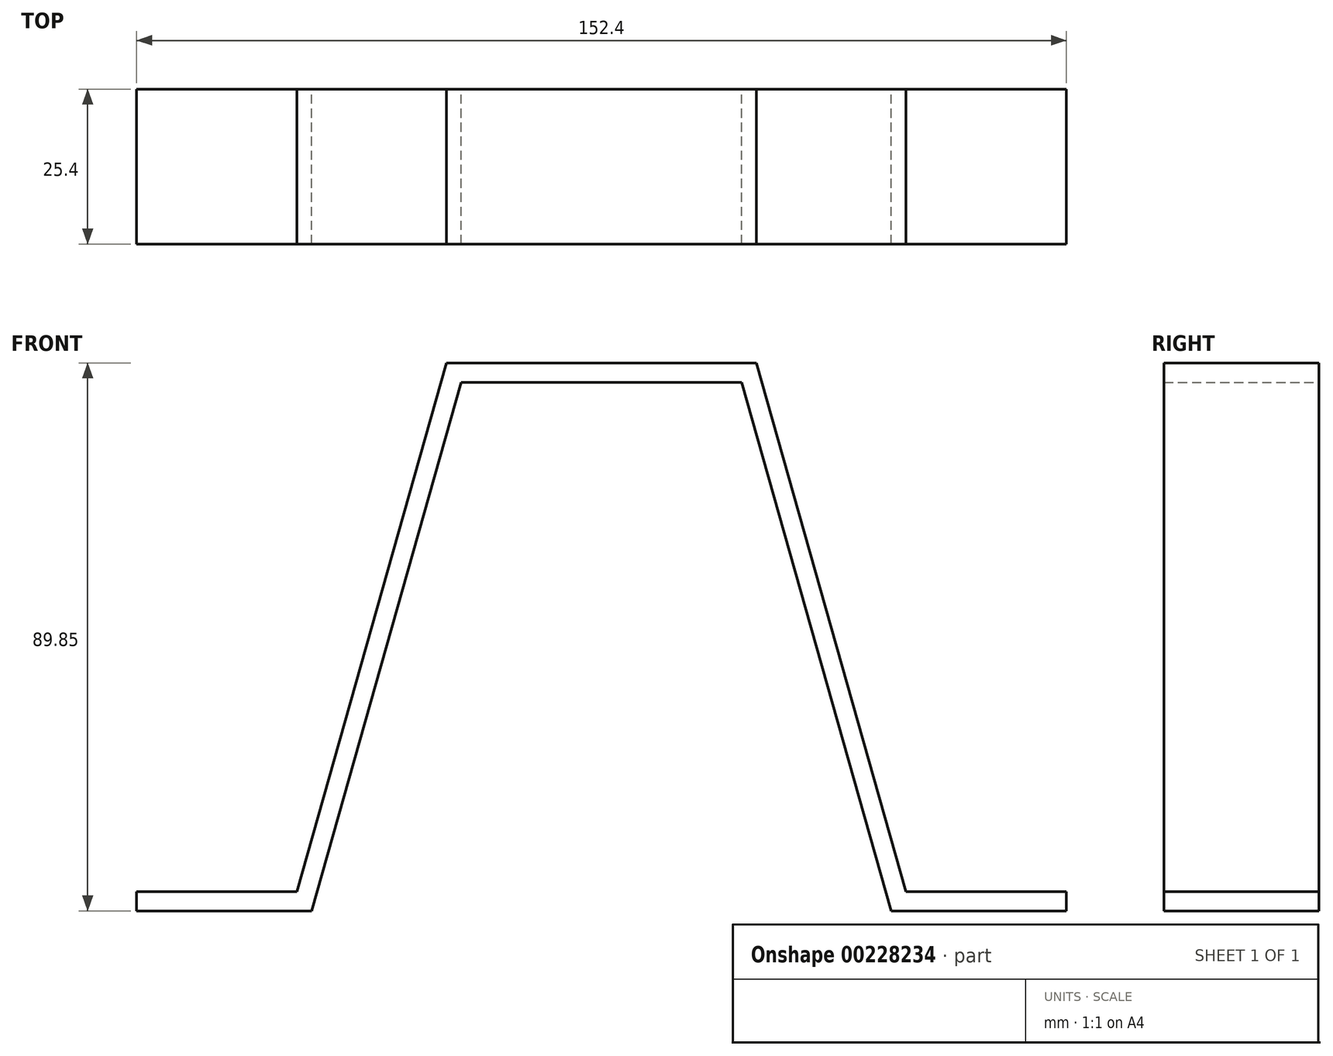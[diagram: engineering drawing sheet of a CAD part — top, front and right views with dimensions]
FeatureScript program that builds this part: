
annotation { "Feature Type Name" : "Feature", "Feature Type Description" : "" }
export const myFeature = defineFeature(function(context is Context, id is Id, definition is map)
    precondition{}
    {
        {
            var Q0;
            Q0=qCreatedBy(makeId("Front.planeOp"),FACE);
            var sketch = newSketch(context, id + "F0", { "sketchPlane" : qUnion([Q0])});
            skLineSegment(sketch, "E0", {"start": v(0, 0) * mm, "end": v(50.8, 0) * mm});
            skLineSegment(sketch, "E1", {"start": v(0, 0) * mm, "end": v(0, 89.85) * mm});
            skLineSegment(sketch, "E2", {"start": v(0, 89.85) * mm, "end": v(25.4, 89.85) * mm});
            skLineSegment(sketch, "E3", {"start": v(25.4, 89.85) * mm, "end": v(50.8, 0) * mm});
            skLineSegment(sketch, "E4.MirrorCS", {"start": v(0, 0) * mm, "end": v(-50.8, 0) * mm});
            skLineSegment(sketch, "E5.MirrorCS", {"start": v(-25.4, 89.85) * mm, "end": v(-50.8, 0) * mm});
            skLineSegment(sketch, "E6.MirrorCS", {"start": v(0, 89.85) * mm, "end": v(-25.4, 89.85) * mm});
            skLineSegment(sketch, "E7.0", {"start": v(-23, 86.68) * mm, "end": v(-47.75, -0.87) * mm});
            skLineSegment(sketch, "E7.1", {"start": v(0, 86.68) * mm, "end": v(-23, 86.68) * mm});
            skLineSegment(sketch, "E7.2", {"start": v(0, 86.68) * mm, "end": v(23, 86.68) * mm});
            skLineSegment(sketch, "E7.3", {"start": v(23, 86.68) * mm, "end": v(60.38, -45.54) * mm});
            skSolve(sketch);
        }
        {
            var Q0;
            {var subQ1=sQuery(id+"F0.wireOp",EDGE,"E5.MirrorCS");Q0=makeQuery(id+"F0.imprint","IMPRINT",FACE,{"disambiguationData":[TD([[makeQuery(id+"F0.imprint","IMPRINT",EDGE,{"derivedFrom":subQ1}),1.0]])]});}
            var Q1;
            {var subQ2=sQuery(id+"F0.wireOp",EDGE,"E2");Q1=makeQuery(id+"F0.imprint","IMPRINT",FACE,{"disambiguationData":[TD([[makeQuery(id+"F0.imprint","IMPRINT",EDGE,{"derivedFrom":subQ2}),-1.0]])]});}
            extrude(context, id + "F1", {"entities" : qUnion([Q0, Q1]), "depth" : 25.4 * mm});
        }
        {
            var Q0;
            Q0=qCreatedBy(makeId("Top.planeOp"),FACE);
            var sketch = newSketch(context, id + "F2", { "sketchPlane" : qUnion([Q0])});
            skLineSegment(sketch, "E8", {"start": v(0, 0) * mm, "end": v(-47.63, 0) * mm});
            skLineSegment(sketch, "E9.bottom", {"start": v(-47.63, 0) * mm, "end": v(-76.2, 0) * mm});
            skLineSegment(sketch, "E9.top", {"start": v(-47.62, -25.4) * mm, "end": v(-76.2, -25.4) * mm});
            skLineSegment(sketch, "E9.left", {"start": v(-47.63, 0) * mm, "end": v(-47.62, -25.4) * mm});
            skLineSegment(sketch, "E9.right", {"start": v(-76.2, 0) * mm, "end": v(-76.2, -25.4) * mm});
            skLineSegment(sketch, "E10.MirrorCS", {"start": v(47.63, 0) * mm, "end": v(47.63, -25.4) * mm});
            skLineSegment(sketch, "E11.MirrorCS", {"start": v(47.63, 0) * mm, "end": v(76.2, 0) * mm});
            skLineSegment(sketch, "E12.MirrorCS", {"start": v(76.2, 0) * mm, "end": v(76.2, -25.4) * mm});
            skLineSegment(sketch, "E13.MirrorCS", {"start": v(47.62, -25.4) * mm, "end": v(76.2, -25.4) * mm});
            skSolve(sketch);
        }
        {
            var Q0;
            Q0 = qSketchRegion(id + "F2", true);
            extrude(context, id + "F3", {"entities" : qUnion([Q0]), "operationType" : NewBodyOperationType.ADD, "depth" : 3.17 * mm});
        }
    });
